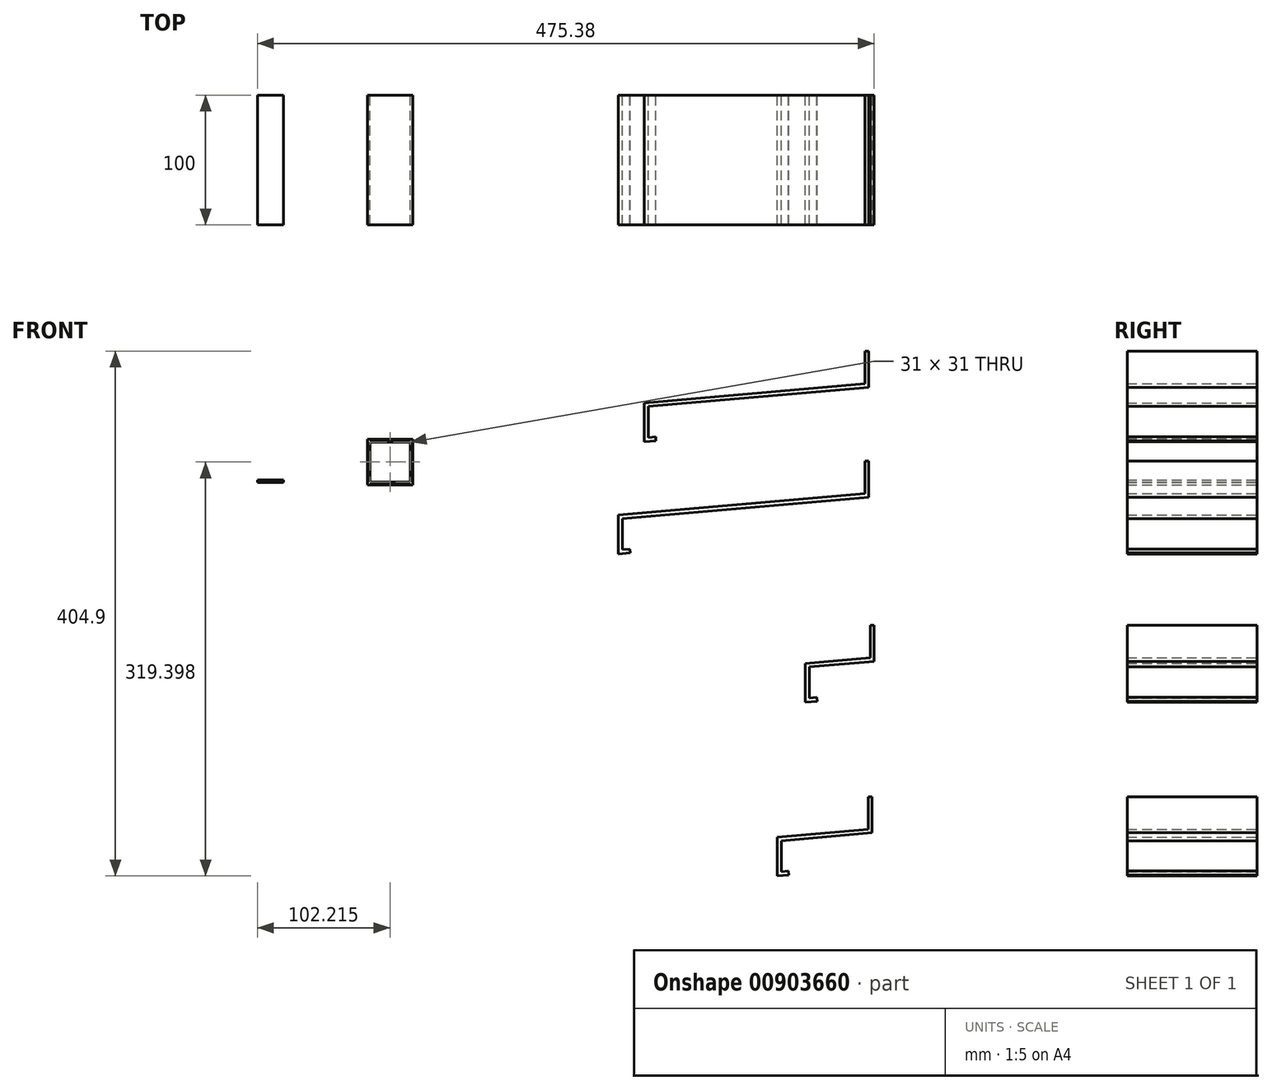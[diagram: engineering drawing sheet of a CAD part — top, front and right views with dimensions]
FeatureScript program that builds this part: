
annotation { "Feature Type Name" : "Feature", "Feature Type Description" : "" }
export const myFeature = defineFeature(function(context is Context, id is Id, definition is map)
    precondition{}
    {
        {
            var Q0;
            Q0=qCreatedBy(makeId("Front.planeOp"),FACE);
            var sketch = newSketch(context, id + "F0", { "sketchPlane" : qUnion([Q0])});
            skLineSegment(sketch, "E0", {"start": v(-628.3, 45.42) * mm, "end": v(-628.3, 20.42) * mm});
            skLineSegment(sketch, "E1", {"start": v(-628.3, 20.42) * mm, "end": v(-798.3, 5.54) * mm});
            skLineSegment(sketch, "E2", {"start": v(-798.3, 5.54) * mm, "end": v(-798.3, -24.46) * mm});
            skLineSegment(sketch, "E3", {"start": v(-798.3, -24.46) * mm, "end": v(-789.33, -23.67) * mm});
            skLineSegment(sketch, "E4", {"start": v(-976.8, -22.58) * mm, "end": v(-1011.8, -22.58) * mm});
            skLineSegment(sketch, "E5", {"start": v(-1011.8, -22.58) * mm, "end": v(-1011.8, -57.58) * mm});
            skLineSegment(sketch, "E6", {"start": v(-1011.8, -57.58) * mm, "end": v(-976.8, -57.58) * mm});
            skLineSegment(sketch, "E7", {"start": v(-976.8, -22.58) * mm, "end": v(-976.8, -57.58) * mm});
            skLineSegment(sketch, "E8.0", {"start": v(-1009.8, -55.58) * mm, "end": v(-978.8, -55.58) * mm});
            skLineSegment(sketch, "E8.1", {"start": v(-1009.8, -24.58) * mm, "end": v(-1009.8, -55.58) * mm});
            skLineSegment(sketch, "E8.2", {"start": v(-978.8, -24.58) * mm, "end": v(-1009.8, -24.58) * mm});
            skLineSegment(sketch, "E8.3", {"start": v(-978.8, -24.58) * mm, "end": v(-978.8, -55.58) * mm});
            skLineSegment(sketch, "E9.bottom", {"start": v(-1076.52, -55.86) * mm, "end": v(-1096.52, -55.86) * mm});
            skLineSegment(sketch, "E9.top", {"start": v(-1076.52, -53.86) * mm, "end": v(-1096.52, -53.86) * mm});
            skLineSegment(sketch, "E9.left", {"start": v(-1076.52, -55.86) * mm, "end": v(-1076.52, -53.86) * mm});
            skLineSegment(sketch, "E9.right", {"start": v(-1096.52, -55.86) * mm, "end": v(-1096.52, -53.86) * mm});
            skLineSegment(sketch, "E10.0", {"start": v(-795.3, -21.18) * mm, "end": v(-789.6, -20.68) * mm});
            skLineSegment(sketch, "E10.1", {"start": v(-795.3, 2.8) * mm, "end": v(-795.3, -21.18) * mm});
            skLineSegment(sketch, "E10.2", {"start": v(-625.3, 17.67) * mm, "end": v(-795.3, 2.8) * mm});
            skLineSegment(sketch, "E10.3", {"start": v(-625.3, 45.42) * mm, "end": v(-625.3, 17.67) * mm});
            skLineSegment(sketch, "E11", {"start": v(-789.6, -20.68) * mm, "end": v(-789.33, -23.67) * mm});
            skLineSegment(sketch, "E12", {"start": v(-625.3, 45.42) * mm, "end": v(-628.3, 45.42) * mm});
            skLineSegment(sketch, "E13", {"start": v(-628.26, -39.37) * mm, "end": v(-628.26, -64.37) * mm});
            skLineSegment(sketch, "E14", {"start": v(-628.26, -64.37) * mm, "end": v(-818.26, -81) * mm});
            skLineSegment(sketch, "E15", {"start": v(-818.26, -81) * mm, "end": v(-818.26, -111) * mm});
            skLineSegment(sketch, "E16", {"start": v(-818.26, -111) * mm, "end": v(-809.3, -110.2) * mm});
            skLineSegment(sketch, "E17.0", {"start": v(-815.26, -107.72) * mm, "end": v(-809.55, -107.22) * mm});
            skLineSegment(sketch, "E17.1", {"start": v(-815.26, -83.74) * mm, "end": v(-815.26, -107.72) * mm});
            skLineSegment(sketch, "E17.2", {"start": v(-625.26, -67.12) * mm, "end": v(-815.26, -83.74) * mm});
            skLineSegment(sketch, "E17.3", {"start": v(-625.26, -39.37) * mm, "end": v(-625.26, -67.12) * mm});
            skLineSegment(sketch, "E18", {"start": v(-809.55, -107.22) * mm, "end": v(-809.3, -110.2) * mm});
            skLineSegment(sketch, "E19", {"start": v(-625.26, -39.37) * mm, "end": v(-628.26, -39.37) * mm});
            skLineSegment(sketch, "E20", {"start": v(-624.14, -166.06) * mm, "end": v(-624.14, -191.06) * mm});
            skLineSegment(sketch, "E21", {"start": v(-624.14, -191.06) * mm, "end": v(-674.14, -195.43) * mm});
            skLineSegment(sketch, "E22", {"start": v(-674.14, -195.43) * mm, "end": v(-674.14, -225.43) * mm});
            skLineSegment(sketch, "E23", {"start": v(-674.14, -225.43) * mm, "end": v(-665.17, -224.65) * mm});
            skLineSegment(sketch, "E24.0", {"start": v(-671.14, -222.16) * mm, "end": v(-665.43, -221.66) * mm});
            skLineSegment(sketch, "E24.1", {"start": v(-671.14, -198.18) * mm, "end": v(-671.14, -222.16) * mm});
            skLineSegment(sketch, "E24.2", {"start": v(-621.14, -193.8) * mm, "end": v(-671.14, -198.18) * mm});
            skLineSegment(sketch, "E24.3", {"start": v(-621.14, -166.06) * mm, "end": v(-621.14, -193.8) * mm});
            skLineSegment(sketch, "E25", {"start": v(-665.43, -221.66) * mm, "end": v(-665.17, -224.65) * mm});
            skLineSegment(sketch, "E26", {"start": v(-621.14, -166.06) * mm, "end": v(-624.14, -166.06) * mm});
            skLineSegment(sketch, "E27", {"start": v(-625.8, -298.35) * mm, "end": v(-625.8, -323.35) * mm});
            skLineSegment(sketch, "E28", {"start": v(-625.8, -323.35) * mm, "end": v(-695.8, -329.48) * mm});
            skLineSegment(sketch, "E29", {"start": v(-695.8, -329.48) * mm, "end": v(-695.8, -359.48) * mm});
            skLineSegment(sketch, "E30", {"start": v(-695.8, -359.48) * mm, "end": v(-686.84, -358.7) * mm});
            skLineSegment(sketch, "E31.0", {"start": v(-692.8, -356.2) * mm, "end": v(-687.1, -355.7) * mm});
            skLineSegment(sketch, "E31.1", {"start": v(-692.8, -332.22) * mm, "end": v(-692.8, -356.2) * mm});
            skLineSegment(sketch, "E31.2", {"start": v(-622.8, -326.1) * mm, "end": v(-692.8, -332.22) * mm});
            skLineSegment(sketch, "E31.3", {"start": v(-622.8, -298.35) * mm, "end": v(-622.8, -326.1) * mm});
            skLineSegment(sketch, "E32", {"start": v(-687.1, -355.7) * mm, "end": v(-686.84, -358.7) * mm});
            skLineSegment(sketch, "E33", {"start": v(-622.8, -298.35) * mm, "end": v(-625.8, -298.35) * mm});
            skSolve(sketch);
        }
        {
            var Q0;
            Q0=makeQuery(id+"F0.imprint","IMPRINT",FACE,{"disambiguationData":[TD([[makeQuery(id+"F0.imprint","IMPRINT",EDGE,{"derivedFrom":sQuery(id+"F0.wireOp",EDGE,"E4")}),1.0]])]});
            extrude(context, id + "F1", {"entities" : qUnion([Q0]), "depth" : 100 * mm, "offsetDistance" : 25 * mm});
        }
        {
            var Q0;
            Q0 = qSketchRegion(id + "F0", true);
            extrude(context, id + "F2", {"entities" : qUnion([Q0]), "operationType" : NewBodyOperationType.ADD, "depth" : 100 * mm, "offsetDistance" : 25 * mm});
        }
    });
